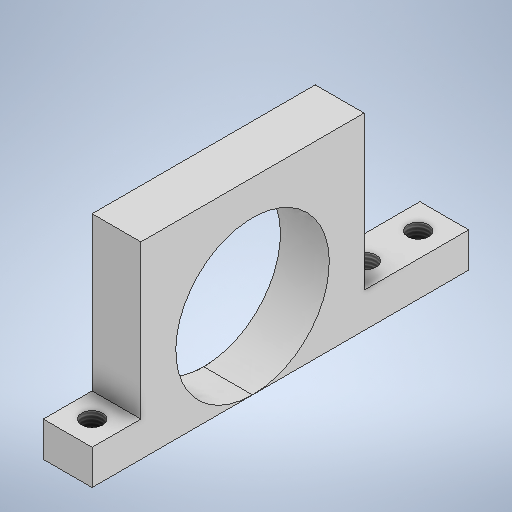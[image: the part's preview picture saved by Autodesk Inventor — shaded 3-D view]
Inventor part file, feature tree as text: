
AUTODESK INVENTOR PART (.ipt)
format: ipt  version: 2025.2 (Build 292293000, 293)  size: 276,992 bytes
history: native  units: in
note: dims shown in document units (in); Inventor stores cm internally (conversion verified against a paired STEP export)
features: extrude x5, sketch x3, thread x3
ambient origin geometry x8: Origin, YZ Plane, XZ Plane, XY Plane, X Axis, Y Axis, Z Axis, Center Point
bodies: Solid1 (feature_tree)
feature tree (11):
  extrude  "Extrusion1"  Depth=0.2756in
  extrude  "Extrusion2"  Depth=0.5906in
  sketch  "Sketch3"  dims[d7=0.2756in d8=0.0in d9=0.1969in d10=0.0in d11=0.1181in d12=0.1181in d14=0.1969in d15=0.0in d16=0.1969in d17=0.0in d18=0.1969in d19=0.0in d20=0.1969in d21=0.0in d22=0.1969in d23=0.0in d24=0.1969in d25=0.0in]
  extrude  "Extrusion3"  Depth=0.1969in TaperAngle=0.0deg
  extrude  "Extrusion4"  Depth=0.1969in
  extrude  "Extrusion5"  Depth=0.1969in
  thread  "Thread1"  [1 undecoded]
  thread  "Thread2"  [1 undecoded]
  thread  "Thread3"  [1 undecoded]
  sketch  "Sketch1"  dims[d0=0.8661in d4=0.2756in]
  sketch  "Sketch2"  dims[d5=0.1969in d6=0.5906in]
note: 3 required parameter values undecoded (feature->parameter linkage not recoverable at this tier; creation-order binding heuristic only, values carry confidence <= 0.55)
